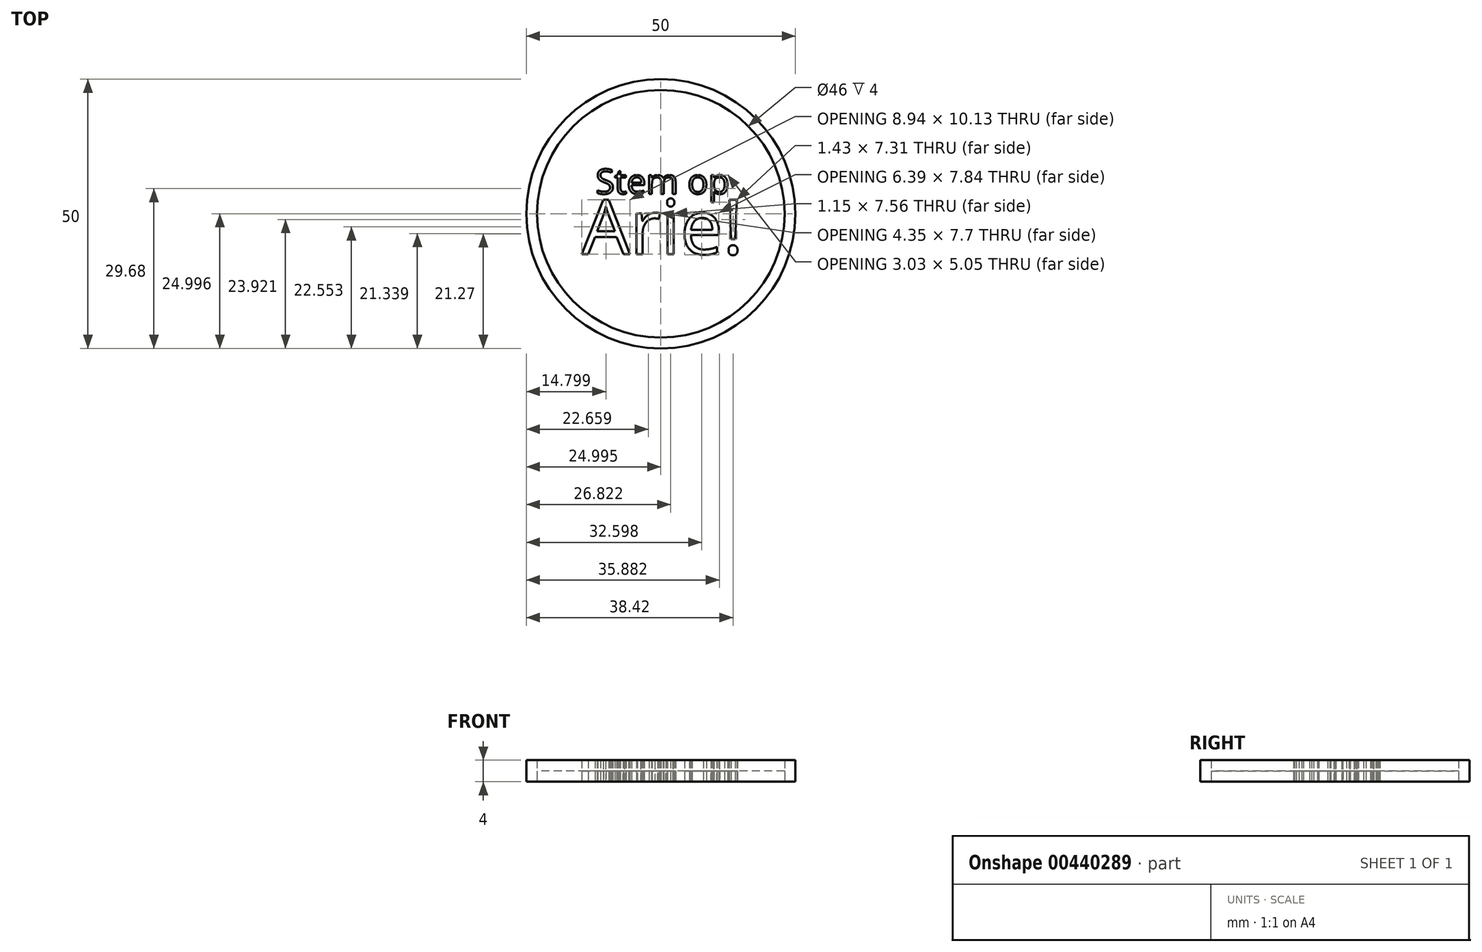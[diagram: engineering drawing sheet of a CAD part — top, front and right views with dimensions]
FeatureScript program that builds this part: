
annotation { "Feature Type Name" : "Feature", "Feature Type Description" : "" }
export const myFeature = defineFeature(function(context is Context, id is Id, definition is map)
    precondition{}
    {
        {
            var Q0;
            Q0=qCreatedBy(makeId("Top.planeOp"),FACE);
            var sketch = newSketch(context, id + "F0", { "sketchPlane" : qUnion([Q0])});
            skCircle(sketch, "E0", {"center": v(-25.11, 15.85) * mm, "radius": 25 * mm});
            skText(sketch, "E1", { "text": "Stem op", "fontName": "OpenSans-Regular.ttf"});
            skText(sketch, "E2", { "text": "Arie!", "fontName": "OpenSans-Regular.ttf"});
            skCircle(sketch, "E3", {"center": v(-25.11, 15.85) * mm, "radius": 23 * mm});
            const initialGuessF0  = {"E1": [-0.03724, 0.01955, 1, 0, 0.00463], "E2": [-0.03978, 0.00834, 1, 0, 0.01017]};
            skSetInitialGuess(sketch, initialGuessF0);
            skSolve(sketch);
        }
        {
            var Q0;
            Q0 = qSketchRegion(id + "F0", true);
            var Q1;
            Q1=makeQuery(id+"F0.imprint","IMPRINT",FACE,{"disambiguationData":[TD([[makeQuery(id+"F0.imprint","IMPRINT",EDGE,{"derivedFrom":sQuery(id+"F0.wireOp",EDGE,"E1.sketch_text.stroke-0")}),-1.0]])]});
            var Q2;
            Q2=makeQuery(id+"F0.imprint","IMPRINT",FACE,{"disambiguationData":[TD([[makeQuery(id+"F0.imprint","IMPRINT",EDGE,{"derivedFrom":sQuery(id+"F0.wireOp",EDGE,"E1.sketch_text.stroke-25")}),-1.0]])]});
            var Q3;
            Q3=makeQuery(id+"F0.imprint","IMPRINT",FACE,{"disambiguationData":[TD([[makeQuery(id+"F0.imprint","IMPRINT",EDGE,{"derivedFrom":sQuery(id+"F0.wireOp",EDGE,"E1.sketch_text.stroke-44")}),-1.0]])]});
            var Q4;
            Q4=makeQuery(id+"F0.imprint","IMPRINT",FACE,{"disambiguationData":[TD([[makeQuery(id+"F0.imprint","IMPRINT",EDGE,{"derivedFrom":sQuery(id+"F0.wireOp",EDGE,"E1.sketch_text.stroke-63")}),-1.0]])]});
            var Q5;
            Q5=makeQuery(id+"F0.imprint","IMPRINT",FACE,{"disambiguationData":[TD([[makeQuery(id+"F0.imprint","IMPRINT",EDGE,{"derivedFrom":sQuery(id+"F0.wireOp",EDGE,"E1.sketch_text.stroke-91")}),-1.0]])]});
            var Q6;
            Q6=makeQuery(id+"F0.imprint","IMPRINT",FACE,{"disambiguationData":[TD([[makeQuery(id+"F0.imprint","IMPRINT",EDGE,{"derivedFrom":sQuery(id+"F0.wireOp",EDGE,"E1.sketch_text.stroke-108")}),-1.0]])]});
            var Q7;
            Q7=makeQuery(id+"F0.imprint","IMPRINT",FACE,{"disambiguationData":[TD([[makeQuery(id+"F0.imprint","IMPRINT",EDGE,{"derivedFrom":sQuery(id+"F0.wireOp",EDGE,"E2.sketch_text.stroke-0")}),-1.0]])]});
            var Q8;
            Q8=makeQuery(id+"F0.imprint","IMPRINT",FACE,{"disambiguationData":[TD([[makeQuery(id+"F0.imprint","IMPRINT",EDGE,{"derivedFrom":sQuery(id+"F0.wireOp",EDGE,"E2.sketch_text.stroke-13")}),-1.0]])]});
            var Q9;
            Q9=makeQuery(id+"F0.imprint","IMPRINT",FACE,{"disambiguationData":[TD([[makeQuery(id+"F0.imprint","IMPRINT",EDGE,{"derivedFrom":sQuery(id+"F0.wireOp",EDGE,"E2.sketch_text.stroke-30")}),-1.0]])]});
            var Q10;
            Q10=makeQuery(id+"F0.imprint","IMPRINT",FACE,{"disambiguationData":[TD([[makeQuery(id+"F0.imprint","IMPRINT",EDGE,{"derivedFrom":sQuery(id+"F0.wireOp",EDGE,"E2.sketch_text.stroke-26")}),-1.0]])]});
            var Q11;
            Q11=makeQuery(id+"F0.imprint","IMPRINT",FACE,{"disambiguationData":[TD([[makeQuery(id+"F0.imprint","IMPRINT",EDGE,{"derivedFrom":sQuery(id+"F0.wireOp",EDGE,"E2.sketch_text.stroke-38")}),-1.0]])]});
            var Q12;
            Q12=makeQuery(id+"F0.imprint","IMPRINT",FACE,{"disambiguationData":[TD([[makeQuery(id+"F0.imprint","IMPRINT",EDGE,{"derivedFrom":sQuery(id+"F0.wireOp",EDGE,"E2.sketch_text.stroke-57")}),-1.0]])]});
            var Q13;
            Q13=makeQuery(id+"F0.imprint","IMPRINT",FACE,{"disambiguationData":[TD([[makeQuery(id+"F0.imprint","IMPRINT",EDGE,{"derivedFrom":sQuery(id+"F0.wireOp",EDGE,"E2.sketch_text.stroke-61")}),-1.0]])]});
            extrude(context, id + "F1", {"entities" : qUnion([Q0, Q1, Q2, Q3, Q4, Q5, Q6, Q7, Q8, Q9, Q10, Q11, Q12, Q13]), "depth" : 4 * mm});
        }
        {
            var Q0;
            Q0=makeQuery(id+"F0.imprint","IMPRINT",FACE,{"disambiguationData":[TD([[makeQuery(id+"F0.imprint","IMPRINT",EDGE,{"derivedFrom":sQuery(id+"F0.wireOp",EDGE,"E1.sketch_text.stroke-0")}),1.0]])]});
            var Q1;
            Q1=makeQuery(id+"F0.imprint","IMPRINT",FACE,{"disambiguationData":[TD([[makeQuery(id+"F0.imprint","IMPRINT",EDGE,{"derivedFrom":sQuery(id+"F0.wireOp",EDGE,"E2.sketch_text.stroke-8")}),1.0]])]});
            var Q2;
            Q2=makeQuery(id+"F0.imprint","IMPRINT",FACE,{"disambiguationData":[TD([[makeQuery(id+"F0.imprint","IMPRINT",EDGE,{"derivedFrom":sQuery(id+"F0.wireOp",EDGE,"E2.sketch_text.stroke-52")}),1.0]])]});
            var Q3;
            Q3=makeQuery(id+"F0.imprint","IMPRINT",FACE,{"disambiguationData":[TD([[makeQuery(id+"F0.imprint","IMPRINT",EDGE,{"derivedFrom":sQuery(id+"F0.wireOp",EDGE,"E1.sketch_text.stroke-100")}),1.0]])]});
            var Q4;
            Q4=makeQuery(id+"F0.imprint","IMPRINT",FACE,{"disambiguationData":[TD([[makeQuery(id+"F0.imprint","IMPRINT",EDGE,{"derivedFrom":sQuery(id+"F0.wireOp",EDGE,"E1.sketch_text.stroke-124")}),1.0]])]});
            var Q5;
            Q5=makeQuery(id+"F0.imprint","IMPRINT",FACE,{"disambiguationData":[TD([[makeQuery(id+"F0.imprint","IMPRINT",EDGE,{"derivedFrom":sQuery(id+"F0.wireOp",EDGE,"E1.sketch_text.stroke-58")}),1.0]])]});
            extrude(context, id + "F2", {"entities" : qUnion([Q0, Q1, Q2, Q3, Q4, Q5]), "depth" : 2 * mm});
        }
    });
